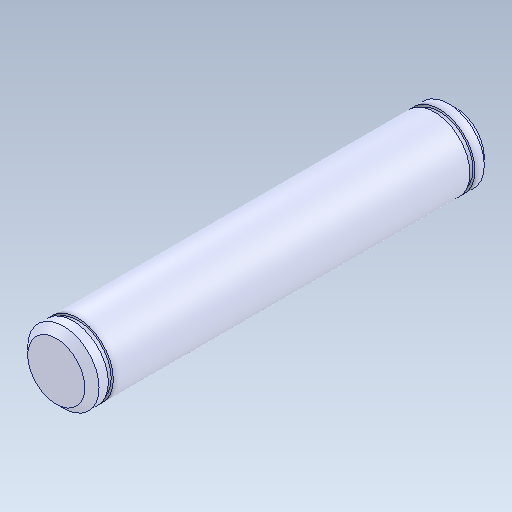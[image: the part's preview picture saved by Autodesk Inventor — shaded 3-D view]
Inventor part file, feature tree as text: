
AUTODESK INVENTOR PART (.ipt)
format: ipt  version: 2021 (Build 250183000, 183)  size: 117,248 bytes
history: mixed  units: mm
features: other x1, chamfer x1, imported_body x1
ambient origin geometry x8: Origin, YZ Plane, XZ Plane, XY Plane, X Axis, Y Axis, Z Axis, Center Point
bodies: Body1 (imported_parasolid)
feature tree (3):
  other  "Sólido1"
  chamfer  "Chamfer1"  [1 undecoded]
  imported_body  NMx_Import_Brep_tag  [imported B-rep: ~13 faces, bbox_mm=[1.0, 0.0, 56.0]]
note: 1 required parameter value undecoded (feature->parameter linkage not recoverable at this tier; creation-order binding heuristic only, values carry confidence <= 0.55)
